# Revit family: FP-Revit20-en-OM30NDTDB1-OM30NDTDX1-OM30NDLX1-ConvectionSpeedOven-0-90003632A-US-CA (2)
name_source: partatom
category: Specialty Equipment
units: mm (PartAtom-declared; Revit-internal decimal feet)

## family parameters
Always vertical = Yes
Cut with Voids When Loaded = Yes
Part Type = Normal
Room Calculation Point = No
Round Connector Dimension = Use Diameter
Shared = No
Work Plane-Based = No

## types (3) — shared parameters
Cavity - Depth = 570 mm  [stored 1.87008 ft]
Cavity - Height = 440 mm  [stored 1.44357 ft]
Cavity - Width = 724 mm  [stored 2.37533 ft]
Chassis - Depth = 545 mm  [stored 1.78806 ft]
Chassis - Height = 435 mm  [stored 1.42717 ft]
Chassis - Width = 720 mm  [stored 2.3622 ft]
Connector Description = 208 or 240 V, 60 Hz, 20A
Description = Combination Steam Oven, 30"
Manufacturer = Fisher & Paykel Appliances
Material - Chassis = Fisher & Paykel - Aluminium
Material - Clearance = Fisher & Paykel - Clearance Required (Cutout)
Material - Door Clearance = Fisher & Paykel - Clearance Required
Material - Glass = Fisher & Paykel - Glass, Black
Product - Depth (excluding handles and dials) = 565 mm  [stored 1.85367 ft]
Product - Width = 760 mm  [stored 2.49344 ft]
Product -Height = 458 mm  [stored 1.50262 ft]
URL = www.fisherpaykel.com
zero-valued in all types: Default Elevation

## per-type parameters (varying)
| type | Material - Dial | Material - Handle | Material - Trim | Model |
| OM30NDTDB1 (Black) | Fisher & Paykel - Black | Fisher & Paykel - Black | Fisher & Paykel - Black | OM30NDTDB1
OM30NDTDB1 |
| OM30NDTDX1 (Stainless Steel) | Fisher & Paykel - Stainless Steel | Fisher & Paykel - Stainless Steel | Fisher & Paykel - Stainless Steel | OM30NDTDX1 |
| OM30NDLX1 (Stainless steel) | Fisher & Paykel - Stainless Steel | Fisher & Paykel - Stainless Steel | Fisher & Paykel - Stainless Steel | OM30NDTDX1 |

note: [stored X ft] marks values corroborated as IEEE doubles in the binary element streams (Revit-internal decimal feet)

## geometry (parser evidence)
native form markers: Sweep x23
no freeform markers — native parametric forms only
